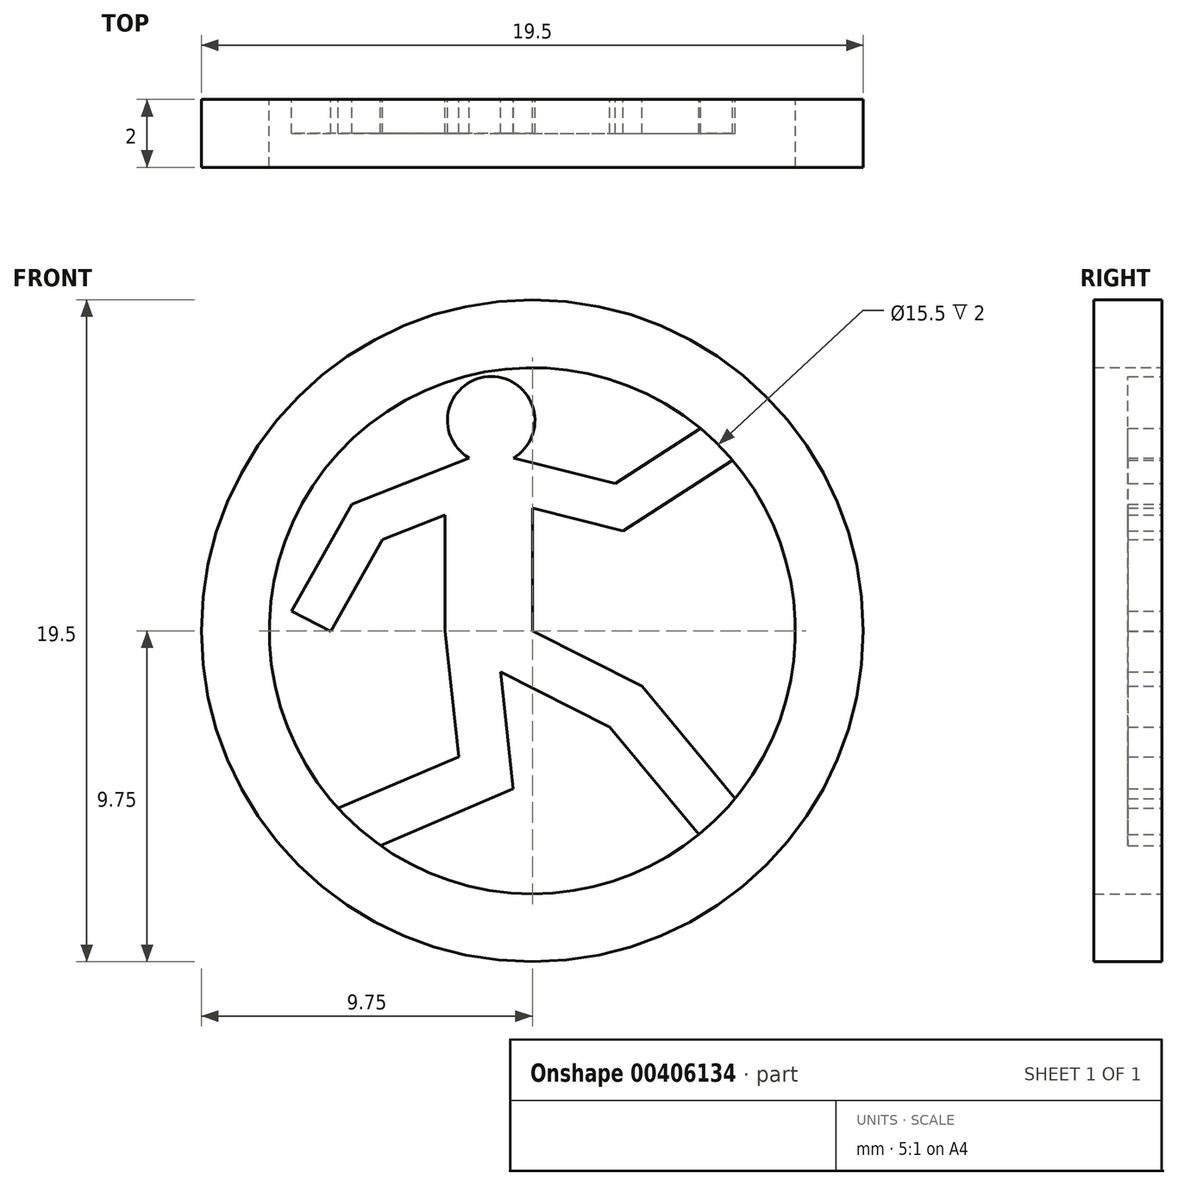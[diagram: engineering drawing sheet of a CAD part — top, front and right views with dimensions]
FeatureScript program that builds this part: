
annotation { "Feature Type Name" : "Feature", "Feature Type Description" : "" }
export const myFeature = defineFeature(function(context is Context, id is Id, definition is map)
    precondition{}
    {
        {
            var Q0;
            Q0=qCreatedBy(makeId("Front.planeOp"),FACE);
            var sketch = newSketch(context, id + "F0", { "sketchPlane" : qUnion([Q0])});
            skCircle(sketch, "E0", {"center": v(0, 0) * mm, "radius": 9.75 * mm});
            skCircle(sketch, "E1.0", {"center": v(0, 0) * mm, "radius": 7.75 * mm});
            skLineSegment(sketch, "E2", {"start": v(-4.48, -6.32) * mm, "end": v(-0.56, -4.65) * mm});
            skLineSegment(sketch, "E3", {"start": v(-0.56, -4.65) * mm, "end": v(-0.94, -1.2) * mm});
            skLineSegment(sketch, "E4.0", {"start": v(-5.72, -5.23) * mm, "end": v(-2.17, -3.7) * mm});
            skLineSegment(sketch, "E5.0", {"start": v(-2.17, -3.7) * mm, "end": v(-2.58, 0) * mm});
            skLineSegment(sketch, "E6", {"start": v(0, 0) * mm, "end": v(0, 3.61) * mm});
            skLineSegment(sketch, "E7", {"start": v(0, 3.61) * mm, "end": v(2.67, 2.95) * mm});
            skLineSegment(sketch, "E8", {"start": v(2.67, 2.95) * mm, "end": v(5.9, 5.02) * mm});
            skLineSegment(sketch, "E9.0", {"start": v(2.44, 4.34) * mm, "end": v(4.95, 5.96) * mm});
            skLineSegment(sketch, "E10", {"start": v(-2.58, 0) * mm, "end": v(-2.58, 3.42) * mm});
            skLineSegment(sketch, "E11", {"start": v(-2.58, 3.42) * mm, "end": v(-4.42, 2.7) * mm});
            skLineSegment(sketch, "E12", {"start": v(-4.42, 2.7) * mm, "end": v(-5.94, -0.02) * mm});
            skLineSegment(sketch, "E13.0", {"start": v(-5.32, 3.73) * mm, "end": v(-7.1, 0.58) * mm});
            skLineSegment(sketch, "E14", {"start": v(-7.1, 0.58) * mm, "end": v(-5.94, -0.02) * mm});
            skLineSegment(sketch, "E15.0", {"start": v(-1.87, 5.1) * mm, "end": v(-5.32, 3.73) * mm});
            skLineSegment(sketch, "E16.0", {"start": v(-0.56, 5.1) * mm, "end": v(2.44, 4.34) * mm});
            skCircle(sketch, "E17", {"center": v(-1.21, 6.2) * mm, "radius": 1.29 * mm});
            skPoint(sketch, "E17.third.point", {"position": v(-1.4, 7.48) * mm});
            skLineSegment(sketch, "E18", {"start": v(0, 0) * mm, "end": v(3.23, -1.64) * mm});
            skLineSegment(sketch, "E19", {"start": v(3.23, -1.64) * mm, "end": v(5.97, -4.94) * mm});
            skLineSegment(sketch, "E20.0", {"start": v(2.27, -2.83) * mm, "end": v(4.9, -6) * mm});
            skLineSegment(sketch, "E21.0", {"start": v(-0.94, -1.2) * mm, "end": v(2.27, -2.83) * mm});
            skSolve(sketch);
        }
        {
            var Q0;
            Q0=makeQuery(id+"F0.imprint","IMPRINT",FACE,{"disambiguationData":[TD([[makeQuery(id+"F0.imprint","IMPRINT",EDGE,{"derivedFrom":sQuery(id+"F0.wireOp",EDGE,"E0")}),1.0]])]});
            extrude(context, id + "F1", {"entities" : qUnion([Q0]), "depth" : 2 * mm});
        }
        {
            var Q0;
            {var subQ9=sQuery(id+"F0.wireOp",EDGE,"E2");Q0=makeQuery(id+"F0.imprint","IMPRINT",FACE,{"disambiguationData":[TD([[makeQuery(id+"F0.imprint","IMPRINT",EDGE,{"derivedFrom":subQ9}),1.0]])]});}
            var Q1;
            {var subQ0=sQuery(id+"F0.wireOp",EDGE,"E17");var subQ1=makeQuery(id+"F0.imprint","INTERSECT",VERTEX,{"derivedFrom":[sQuery(id+"F0.wireOp",EDGE,"E15.0"),subQ0]});Q1=makeQuery(id+"F0.imprint","IMPRINT",FACE,{"disambiguationData":[TD([[makeQuery(id+"F0.imprint","IMPRINT",EDGE,{"disambiguationData":[TD([[subQ1,-1.0]])],"derivedFrom":subQ0}),1.0]])]});}
            extrude(context, id + "F2", {"entities" : qUnion([Q0, Q1]), "operationType" : NewBodyOperationType.ADD, "depth" : 1 * mm});
        }
    });
